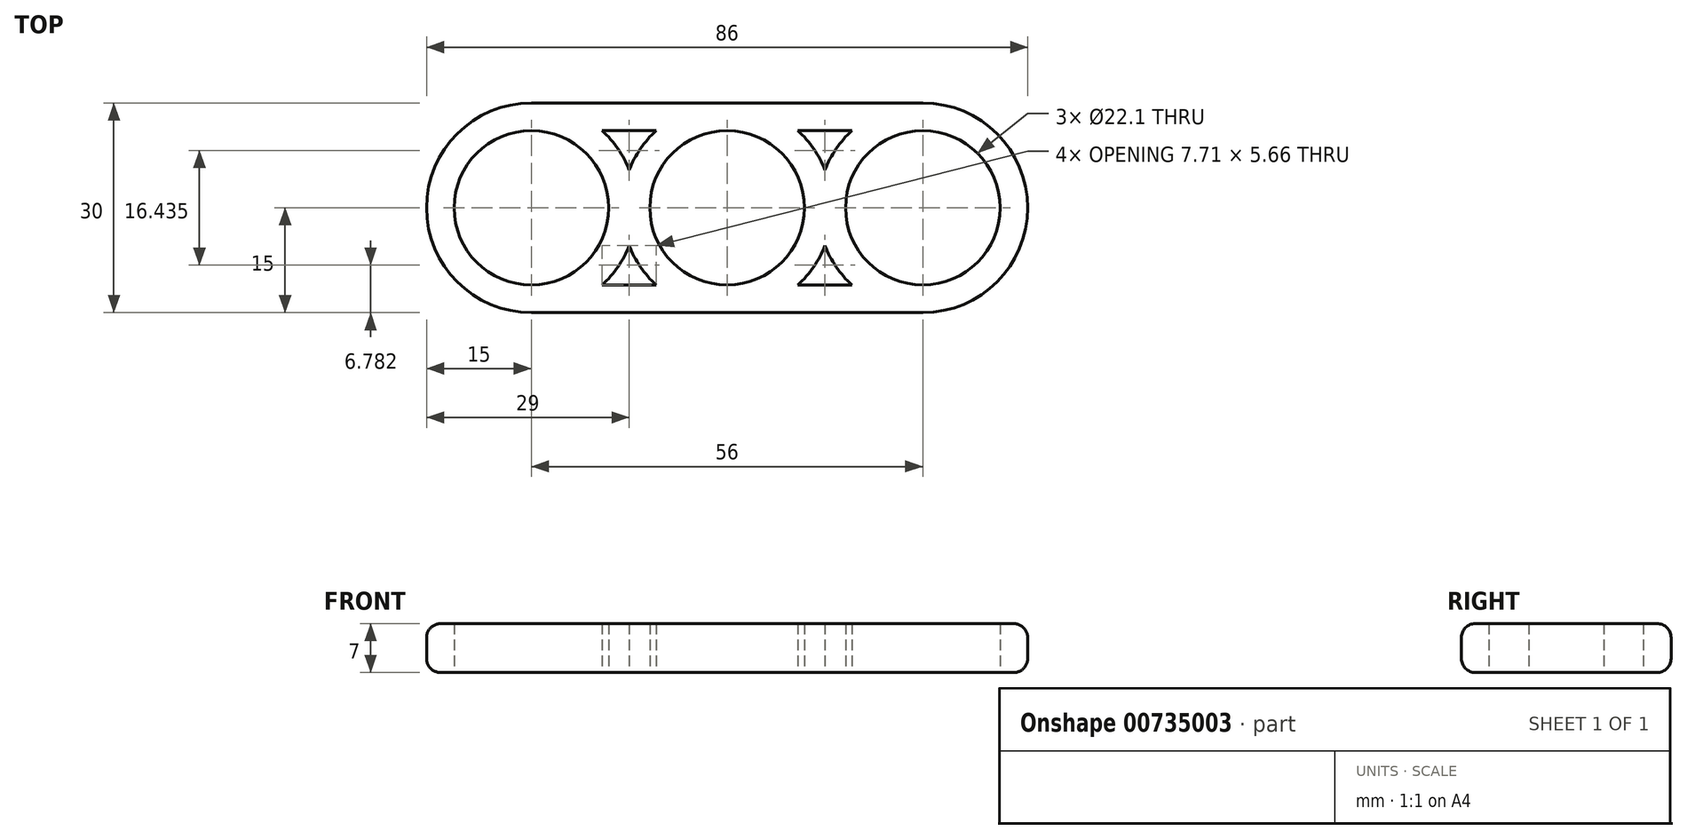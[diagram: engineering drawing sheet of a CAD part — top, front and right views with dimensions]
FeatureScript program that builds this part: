
annotation { "Feature Type Name" : "Feature", "Feature Type Description" : "" }
export const myFeature = defineFeature(function(context is Context, id is Id, definition is map)
    precondition{}
    {
        {
            var Q0;
            Q0=qCreatedBy(makeId("Top.planeOp"),FACE);
            var sketch = newSketch(context, id + "F0", { "sketchPlane" : qUnion([Q0])});
            skCircle(sketch, "E0", {"center": v(0, 0) * mm, "radius": 11.05 * mm});
            skCircle(sketch, "E1", {"center": v(0, 0) * mm, "radius": 15 * mm});
            skCircle(sketch, "E2", {"center": v(-28, 0) * mm, "radius": 11.05 * mm});
            skCircle(sketch, "E3", {"center": v(-28, 0) * mm, "radius": 15 * mm});
            skCircle(sketch, "E4", {"center": v(28, 0) * mm, "radius": 11.05 * mm});
            skCircle(sketch, "E5", {"center": v(28, 0) * mm, "radius": 15 * mm});
            skLineSegment(sketch, "E6", {"start": v(-28, 0) * mm, "end": v(-28, -15) * mm, "construction": true});
            skLineSegment(sketch, "E7", {"start": v(-28, 0) * mm, "end": v(-28, 15) * mm, "construction": true});
            skLineSegment(sketch, "E8", {"start": v(28, 0) * mm, "end": v(28, 15) * mm, "construction": true});
            skLineSegment(sketch, "E9", {"start": v(28, 0) * mm, "end": v(28, -15) * mm, "construction": true});
            skLineSegment(sketch, "E10", {"start": v(-28, -15) * mm, "end": v(28, -15) * mm});
            skLineSegment(sketch, "E11", {"start": v(-28, 15) * mm, "end": v(28, 15) * mm});
            skPoint(sketch, "E12.endSnap0", {"position": v(28, -7.5) * mm});
            skLineSegment(sketch, "E13", {"start": v(-17.86, -11.05) * mm, "end": v(17.86, -11.05) * mm});
            skLineSegment(sketch, "E14", {"start": v(-17.86, 11.05) * mm, "end": v(17.86, 11.05) * mm});
            skSolve(sketch);
        }
        {
            var Q0;
            Q0=qSketchRegion(id+"F0",true);
            var Q1;
            {var subQ0=sQuery(id+"F0.wireOp",EDGE,"E3");var subQ1=sQuery(id+"F0.wireOp",EDGE,"E1");var subQ2=makeQuery(id+"F0.imprint","INTERSECT",VERTEX,{"disambiguationData":[OD(0.0)],"derivedFrom":[subQ1,subQ0]});Q1=makeQuery(id+"F0.imprint","IMPRINT",FACE,{"disambiguationData":[TD([[makeQuery(id+"F0.imprint","IMPRINT",EDGE,{"disambiguationData":[TD([[subQ2,-1.0]])],"derivedFrom":subQ1}),1.0]])]});}
            var Q2;
            {var subQ4=sQuery(id+"F0.wireOp",EDGE,"E13");var subQ8=sQuery(id+"F0.wireOp",EDGE,"E0");var subQ9=makeQuery(id+"F0.imprint","INTERSECT",VERTEX,{"derivedFrom":[subQ8,subQ4]});Q2=makeQuery(id+"F0.imprint","IMPRINT",FACE,{"disambiguationData":[TD([[makeQuery(id+"F0.imprint","IMPRINT",EDGE,{"disambiguationData":[TD([[subQ9,1.0]])],"derivedFrom":subQ8}),-1.0]])]});}
            var Q3;
            {var subQ0=sQuery(id+"F0.wireOp",EDGE,"E13");var subQ5=sQuery(id+"F0.wireOp",EDGE,"E0");var subQ6=makeQuery(id+"F0.imprint","INTERSECT",VERTEX,{"derivedFrom":[subQ5,subQ0]});Q3=makeQuery(id+"F0.imprint","IMPRINT",FACE,{"disambiguationData":[TD([[makeQuery(id+"F0.imprint","IMPRINT",EDGE,{"disambiguationData":[TD([[subQ6,-1.0]])],"derivedFrom":subQ5}),-1.0]])]});}
            var Q4;
            {var subQ0=sQuery(id+"F0.wireOp",EDGE,"E5");var subQ1=sQuery(id+"F0.wireOp",EDGE,"E1");var subQ2=makeQuery(id+"F0.imprint","INTERSECT",VERTEX,{"disambiguationData":[OD(0.0)],"derivedFrom":[subQ1,subQ0]});Q4=makeQuery(id+"F0.imprint","IMPRINT",FACE,{"disambiguationData":[TD([[makeQuery(id+"F0.imprint","IMPRINT",EDGE,{"disambiguationData":[TD([[subQ2,1.0]])],"derivedFrom":subQ1}),1.0]])]});}
            extrude(context, id + "F1", {"entities" : qUnion([Q0, Q1, Q2, Q3, Q4]), "depth" : 7 * mm, "offsetDistance" : 25 * mm});
        }
        {
            var Q0;
            Q0=makeQuery(id+"F1.opExtrude","CAP_EDGE",EDGE,{"disambiguationData":[OSD([sQuery(id+"F0.wireOp",EDGE,"E11")])],"isStart":false});
            var Q1;
            Q1=makeQuery(id+"F1.opExtrude","CAP_EDGE",EDGE,{"disambiguationData":[OSD([sQuery(id+"F0.wireOp",EDGE,"E10")])],"isStart":true});
            fillet(context, id + "F2", {"entities" : qUnion([Q0, Q1]), "radius" : 2 * mm, "tangentPropagation" : true, "allowEdgeOverflow" : false});
        }
    });
